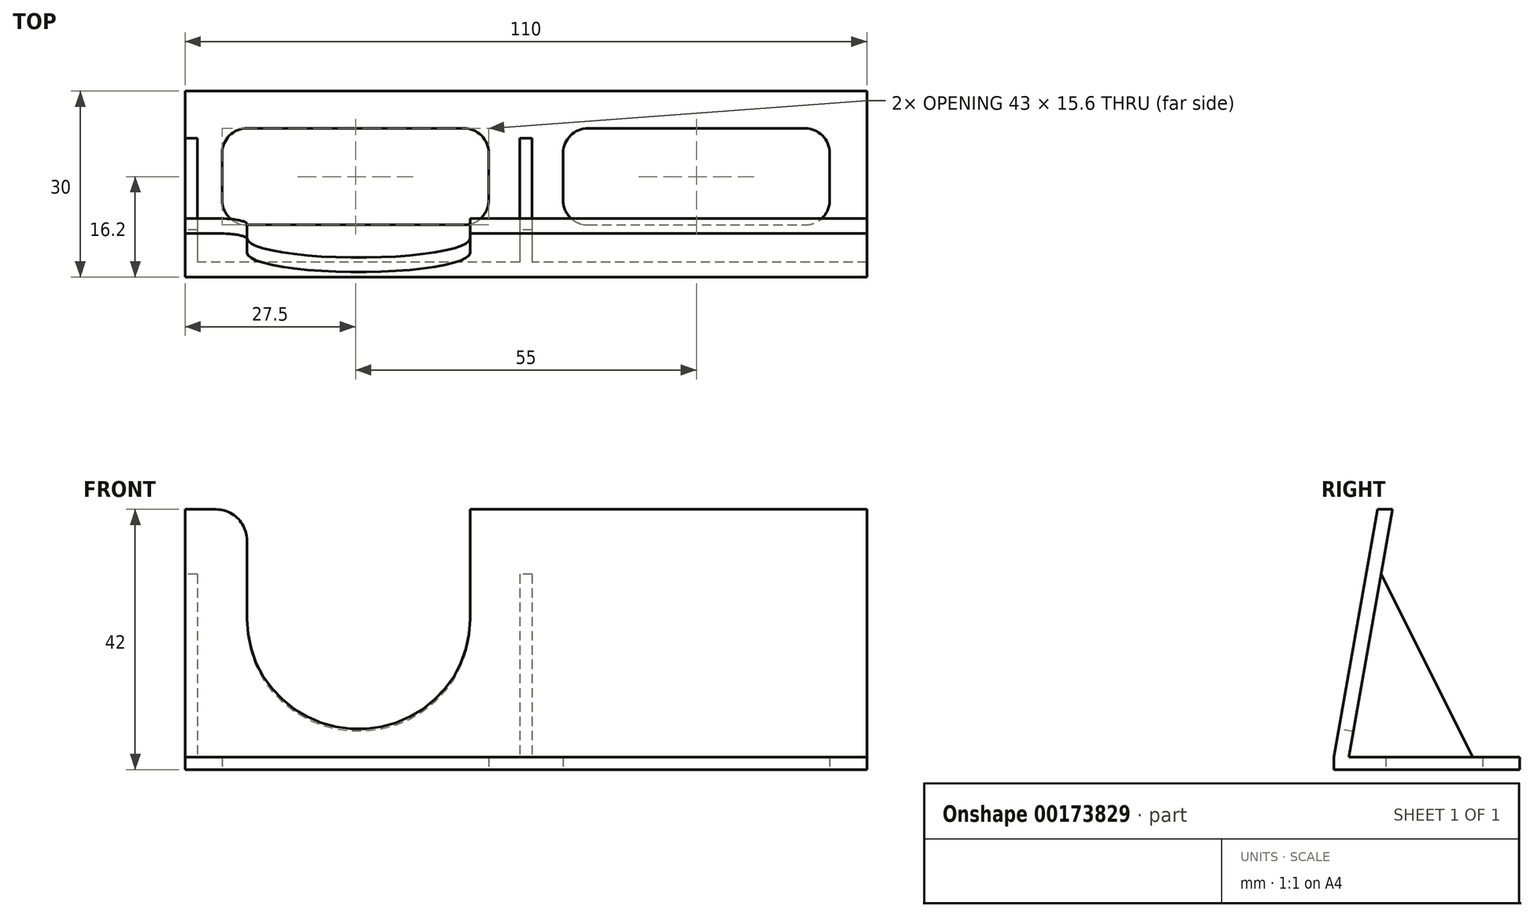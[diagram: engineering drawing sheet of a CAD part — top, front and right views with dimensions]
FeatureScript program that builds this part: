
annotation { "Feature Type Name" : "Feature", "Feature Type Description" : "" }
export const myFeature = defineFeature(function(context is Context, id is Id, definition is map)
    precondition{}
    {
        {
            var Q0;
            Q0=qCreatedBy(makeId("Top.planeOp"),FACE);
            var sketch = newSketch(context, id + "F0", { "sketchPlane" : qUnion([Q0])});
            skLineSegment(sketch, "E0.bottom", {"start": v(55, 15) * mm, "end": v(-55, 15) * mm});
            skLineSegment(sketch, "E0.top", {"start": v(55, -15) * mm, "end": v(-55, -15) * mm});
            skLineSegment(sketch, "E0.left", {"start": v(55, 15) * mm, "end": v(55, -15) * mm});
            skLineSegment(sketch, "E0.right", {"start": v(-55, 15) * mm, "end": v(-55, -15) * mm});
            skPoint(sketch, "E0.middle", {"position": v(0, 0) * mm});
            skSolve(sketch);
        }
        {
            var Q0;
            Q0 = qSketchRegion(id + "F0", true);
            extrude(context, id + "F1", {"entities" : qUnion([Q0]), "depth" : 2 * mm});
        }
        {
            var Q0;
            Q0=qCreatedBy(makeId("Right.planeOp"),FACE);
            var sketch = newSketch(context, id + "F2", { "sketchPlane" : qUnion([Q0])});
            skLineSegment(sketch, "E1.0", {"start": v(-12.6, 2) * mm, "end": v(-15, 2) * mm});
            skLineSegment(sketch, "E2", {"start": v(-15, 2) * mm, "end": v(-7.95, 42) * mm});
            skLineSegment(sketch, "E3", {"start": v(-7.95, 42) * mm, "end": v(-5.55, 42) * mm});
            skLineSegment(sketch, "E4", {"start": v(-5.55, 42) * mm, "end": v(-12.6, 2) * mm});
            skPoint(sketch, "E5.orphan", {"position": v(15, 2) * mm});
            skSolve(sketch);
        }
        {
            var Q0;
            Q0 = qSketchRegion(id + "F2", true);
            var Q1;
            Q1=makeQuery(id+"F1.opExtrude","SWEPT_FACE",FACE,{"disambiguationData":[OSD([sQuery(id+"F0.wireOp",EDGE,"E0.left")])]});
            extrude(context, id + "F3", {"entities" : qUnion([Q0]), "operationType" : NewBodyOperationType.ADD, "endBound" : BoundingType.SYMMETRIC, "endBoundEntityFace" : qUnion([Q1]), "depth" : 110 * mm});
        }
        {
            var Q0;
            Q0=makeQuery(id+"F3.opExtrude","SWEPT_FACE",FACE,{"disambiguationData":[OSD([sQuery(id+"F2.wireOp",EDGE,"E2")])]});
            var sketch = newSketch(context, id + "F4", { "sketchPlane" : qUnion([Q0])});
            skLineSegment(sketch, "E6.0", {"start": v(-9, 39.98) * mm, "end": v(-45, 39.98) * mm, "construction": true});
            skLineSegment(sketch, "E7", {"start": v(-9, 39.98) * mm, "end": v(-9, 21.98) * mm});
            skLineSegment(sketch, "E8", {"start": v(-45, 39.98) * mm, "end": v(-45, 21.98) * mm});
            skArc(sketch, "E9", {"start": v(-45, 21.98) * mm, "mid": v(-27, 3.98) * mm, "end": v(-9, 21.98) * mm});
            skPoint(sketch, "E10.orphan", {"position": v(55, 39.98) * mm});
            skPoint(sketch, "E11.orphan", {"position": v(-55, 39.98) * mm});
            skLineSegment(sketch, "E12", {"start": v(-45, 39.98) * mm, "end": v(-45, 44.98) * mm});
            skLineSegment(sketch, "E13", {"start": v(-45, 44.98) * mm, "end": v(-9, 44.98) * mm});
            skLineSegment(sketch, "E14", {"start": v(-9, 44.98) * mm, "end": v(-9, 39.98) * mm});
            skSolve(sketch);
        }
        {
            var Q0;
            Q0 = qSketchRegion(id + "F4", true);
            extrude(context, id + "F5", {"entities" : qUnion([Q0]), "operationType" : NewBodyOperationType.REMOVE, "endBound" : BoundingType.UP_TO_NEXT, "oppositeDirection" : true, "depth" : 25 * mm});
        }
        {
            var Q0;
            Q0=makeQuery(id+"F3.boolean.opBoolean","MERGE",FACE,{"derivedFrom":[makeQuery(id+"F1.opExtrude","SWEPT_FACE",FACE,{"disambiguationData":[OSD([sQuery(id+"F0.wireOp",EDGE,"E0.right")])]}),makeQuery(id+"F3.opExtrude","CAP_FACE",FACE,{"disambiguationData":[OSD([sQuery(id+"F2.wireOp",EDGE,"E1.0"),sQuery(id+"F2.wireOp",EDGE,"E2"),sQuery(id+"F2.wireOp",EDGE,"E3"),sQuery(id+"F2.wireOp",EDGE,"E4")])],"isStart":true})]});
            var sketch = newSketch(context, id + "F6", { "sketchPlane" : qUnion([Q0])});
            skLineSegment(sketch, "E15.0", {"start": v(-7.4, 2) * mm, "end": v(12.6, 2) * mm});
            skLineSegment(sketch, "E16.0", {"start": v(7.4, 31.54) * mm, "end": v(12.6, 2) * mm});
            skLineSegment(sketch, "E17", {"start": v(-7.4, 2) * mm, "end": v(7.4, 31.54) * mm});
            skPoint(sketch, "E18.orphan", {"position": v(5.55, 42) * mm});
            skPoint(sketch, "E19.orphan", {"position": v(-15, 2) * mm});
            skSolve(sketch);
        }
        {
            var Q0;
            Q0 = qSketchRegion(id + "F6", true);
            extrude(context, id + "F7", {"entities" : qUnion([Q0]), "operationType" : NewBodyOperationType.ADD, "oppositeDirection" : true, "depth" : 2 * mm});
        }
        {
            var Q0;
            Q0=qCreatedBy(makeId("Right.planeOp"),FACE);
            var sketch = newSketch(context, id + "F8", { "sketchPlane" : qUnion([Q0])});
            skLineSegment(sketch, "E20.0", {"start": v(7.4, 2) * mm, "end": v(-7.4, 31.54) * mm});
            skLineSegment(sketch, "E21.0", {"start": v(7.4, 2) * mm, "end": v(-12.6, 2) * mm});
            skLineSegment(sketch, "E22.0", {"start": v(-7.4, 31.54) * mm, "end": v(-12.6, 2) * mm});
            skSolve(sketch);
        }
        {
            var Q0;
            Q0 = qSketchRegion(id + "F8", true);
            extrude(context, id + "F9", {"entities" : qUnion([Q0]), "operationType" : NewBodyOperationType.ADD, "endBound" : BoundingType.SYMMETRIC, "depth" : 2 * mm});
        }
        {
            var Q0;
            Q0=qCreatedBy(makeId("Top.planeOp"),FACE);
            var sketch = newSketch(context, id + "F10", { "sketchPlane" : qUnion([Q0])});
            skLineSegment(sketch, "E23.0", {"start": v(49, 9) * mm, "end": v(6, 9) * mm});
            skLineSegment(sketch, "E24", {"start": v(-49, 9) * mm, "end": v(-49, -6.6) * mm});
            skLineSegment(sketch, "E25", {"start": v(49, 9) * mm, "end": v(49, -6.6) * mm});
            skLineSegment(sketch, "E26.0", {"start": v(-1, -12.6) * mm, "end": v(-53, -12.6) * mm, "construction": true});
            skLineSegment(sketch, "E27", {"start": v(-49, -6.6) * mm, "end": v(-6, -6.6) * mm});
            skPoint(sketch, "E28.0.end.orphan", {"position": v(55, 7.4) * mm});
            skPoint(sketch, "E29.orphan", {"position": v(55, 15) * mm});
            skPoint(sketch, "E30.0.end.orphan", {"position": v(-55, 7.4) * mm});
            skPoint(sketch, "E31.orphan", {"position": v(-55, 15) * mm});
            skLineSegment(sketch, "E32", {"start": v(-6, -6.6) * mm, "end": v(-6, 9) * mm});
            skLineSegment(sketch, "E33", {"start": v(6, 9) * mm, "end": v(6, -6.6) * mm});
            skLineSegment(sketch, "E34.trimOffspring", {"start": v(6, -6.6) * mm, "end": v(49, -6.6) * mm});
            skLineSegment(sketch, "E35.trimOffspring", {"start": v(-6, 9) * mm, "end": v(-49, 9) * mm});
            skSolve(sketch);
        }
        {
            var Q0;
            Q0 = qSketchRegion(id + "F10", true);
            extrude(context, id + "F11", {"entities" : qUnion([Q0]), "operationType" : NewBodyOperationType.REMOVE, "endBound" : BoundingType.UP_TO_NEXT, "depth" : 25 * mm});
        }
        {
            var Q0;
            Q0=makeQuery(id+"F5.boolean.opBoolean","COPY",EDGE,{"derivedFrom":makeQuery(id+"F5.opExtrude","CAP_EDGE",EDGE,{"disambiguationData":[OSD([sQuery(id+"F4.wireOp",EDGE,"E8"),sQuery(id+"F4.wireOp",EDGE,"E12")]),topologyDisambiguationEdgeConnected([makeQuery(id+"F3.opExtrude","SWEPT_FACE",FACE,{"disambiguationData":[OSD([sQuery(id+"F2.wireOp",EDGE,"E3")])]})])],"isStart":false})});
            var Q1;
            Q1=makeQuery(id+"F5.boolean.opBoolean","COPY",EDGE,{"derivedFrom":makeQuery(id+"F5.opExtrude","CAP_EDGE",EDGE,{"disambiguationData":[OSD([sQuery(id+"F4.wireOp",EDGE,"E7"),sQuery(id+"F4.wireOp",EDGE,"E14")]),topologyDisambiguationEdgeConnected([makeQuery(id+"F3.opExtrude","SWEPT_FACE",FACE,{"disambiguationData":[OSD([sQuery(id+"F2.wireOp",EDGE,"E3")])]})])],"isStart":false})});
            var Q2;
            {var subQ2=sQuery(id+"F2.wireOp",EDGE,"E3");var subQ3=sQuery(id+"F4.wireOp",EDGE,"E14");var subQ4=sQuery(id+"F4.wireOp",EDGE,"E7");Q2=makeQuery(id+"Fp0kGsgpF8wRtRn_1.1.F5.boolean.opBoolean","COPY",EDGE,{"derivedFrom":makeQuery(id+"Fp0kGsgpF8wRtRn_1.1.F5.opExtrude","CAP_EDGE",EDGE,{"disambiguationData":[OSD([subQ4,subQ3]),topologyDisambiguationEdgeConnected([makeQuery(id+"F5.boolean.opBoolean","SPLIT",FACE,{"disambiguationData":[TD([makeQuery(id+"F1.opExtrude","SWEPT_FACE",FACE,{"disambiguationData":[OSD([sQuery(id+"F0.wireOp",EDGE,"E0.left")])]})])],"derivedFrom":makeQuery(id+"F3.opExtrude","SWEPT_FACE",FACE,{"disambiguationData":[OSD([subQ2])]})})])],"isStart":false})});}
            var Q3;
            {var subQ2=sQuery(id+"F2.wireOp",EDGE,"E3");Q3=makeQuery(id+"Fp0kGsgpF8wRtRn_1.1.F5.boolean.opBoolean","COPY",EDGE,{"derivedFrom":makeQuery(id+"Fp0kGsgpF8wRtRn_1.1.F5.opExtrude","CAP_EDGE",EDGE,{"disambiguationData":[OSD([sQuery(id+"F4.wireOp",EDGE,"E8"),sQuery(id+"F4.wireOp",EDGE,"E12")]),topologyDisambiguationEdgeConnected([makeQuery(id+"F5.boolean.opBoolean","SPLIT",FACE,{"disambiguationData":[TD([makeQuery(id+"F1.opExtrude","SWEPT_FACE",FACE,{"disambiguationData":[OSD([sQuery(id+"F0.wireOp",EDGE,"E0.left")])]})])],"derivedFrom":makeQuery(id+"F3.opExtrude","SWEPT_FACE",FACE,{"disambiguationData":[OSD([subQ2])]})})])],"isStart":false})});}
            fillet(context, id + "F12", {"entities" : qUnion([Q0, Q1, Q2, Q3]), "radius" : 5 * mm, "tangentPropagation" : true, "allowEdgeOverflow" : false});
        }
        {
            var Q0;
            Q0=makeQuery(id+"F11.boolean.opBoolean","COPY",EDGE,{"derivedFrom":makeQuery(id+"F11.opExtrude","SWEPT_EDGE",EDGE,{"disambiguationData":[OSD([sQuery(id+"F10.wireOp",EDGE,"E24"),sQuery(id+"F10.wireOp",EDGE,"E27")])]})});
            var Q1;
            Q1=makeQuery(id+"F11.boolean.opBoolean","COPY",EDGE,{"derivedFrom":makeQuery(id+"F11.opExtrude","SWEPT_EDGE",EDGE,{"disambiguationData":[OSD([sQuery(id+"F10.wireOp",EDGE,"E25"),sQuery(id+"F10.wireOp",EDGE,"E34.trimOffspring")])]})});
            var Q2;
            Q2=makeQuery(id+"F11.boolean.opBoolean","COPY",EDGE,{"derivedFrom":makeQuery(id+"F11.opExtrude","SWEPT_EDGE",EDGE,{"disambiguationData":[OSD([sQuery(id+"F10.wireOp",EDGE,"E27"),sQuery(id+"F10.wireOp",EDGE,"E32")])]})});
            var Q3;
            Q3=makeQuery(id+"F11.boolean.opBoolean","COPY",EDGE,{"derivedFrom":makeQuery(id+"F11.opExtrude","SWEPT_EDGE",EDGE,{"disambiguationData":[OSD([sQuery(id+"F10.wireOp",EDGE,"E33"),sQuery(id+"F10.wireOp",EDGE,"E34.trimOffspring")])]})});
            var Q4;
            Q4=makeQuery(id+"F11.boolean.opBoolean","COPY",EDGE,{"derivedFrom":makeQuery(id+"F11.opExtrude","SWEPT_EDGE",EDGE,{"disambiguationData":[OSD([sQuery(id+"F10.wireOp",EDGE,"E23.0"),sQuery(id+"F10.wireOp",EDGE,"E33")])]})});
            var Q5;
            Q5=makeQuery(id+"F11.boolean.opBoolean","COPY",EDGE,{"derivedFrom":makeQuery(id+"F11.opExtrude","SWEPT_EDGE",EDGE,{"disambiguationData":[OSD([sQuery(id+"F10.wireOp",EDGE,"E24"),sQuery(id+"F10.wireOp",EDGE,"E35.trimOffspring")])]})});
            var Q6;
            Q6=makeQuery(id+"F11.boolean.opBoolean","COPY",EDGE,{"derivedFrom":makeQuery(id+"F11.opExtrude","SWEPT_EDGE",EDGE,{"disambiguationData":[OSD([sQuery(id+"F10.wireOp",EDGE,"E23.0"),sQuery(id+"F10.wireOp",EDGE,"E25")])]})});
            var Q7;
            Q7=makeQuery(id+"F11.boolean.opBoolean","COPY",EDGE,{"derivedFrom":makeQuery(id+"F11.opExtrude","SWEPT_EDGE",EDGE,{"disambiguationData":[OSD([sQuery(id+"F10.wireOp",EDGE,"E32"),sQuery(id+"F10.wireOp",EDGE,"E35.trimOffspring")])]})});
            fillet(context, id + "F13", {"entities" : qUnion([Q0, Q1, Q2, Q3, Q4, Q5, Q6, Q7]), "radius" : 4 * mm, "tangentPropagation" : true, "allowEdgeOverflow" : false});
        }
    });
